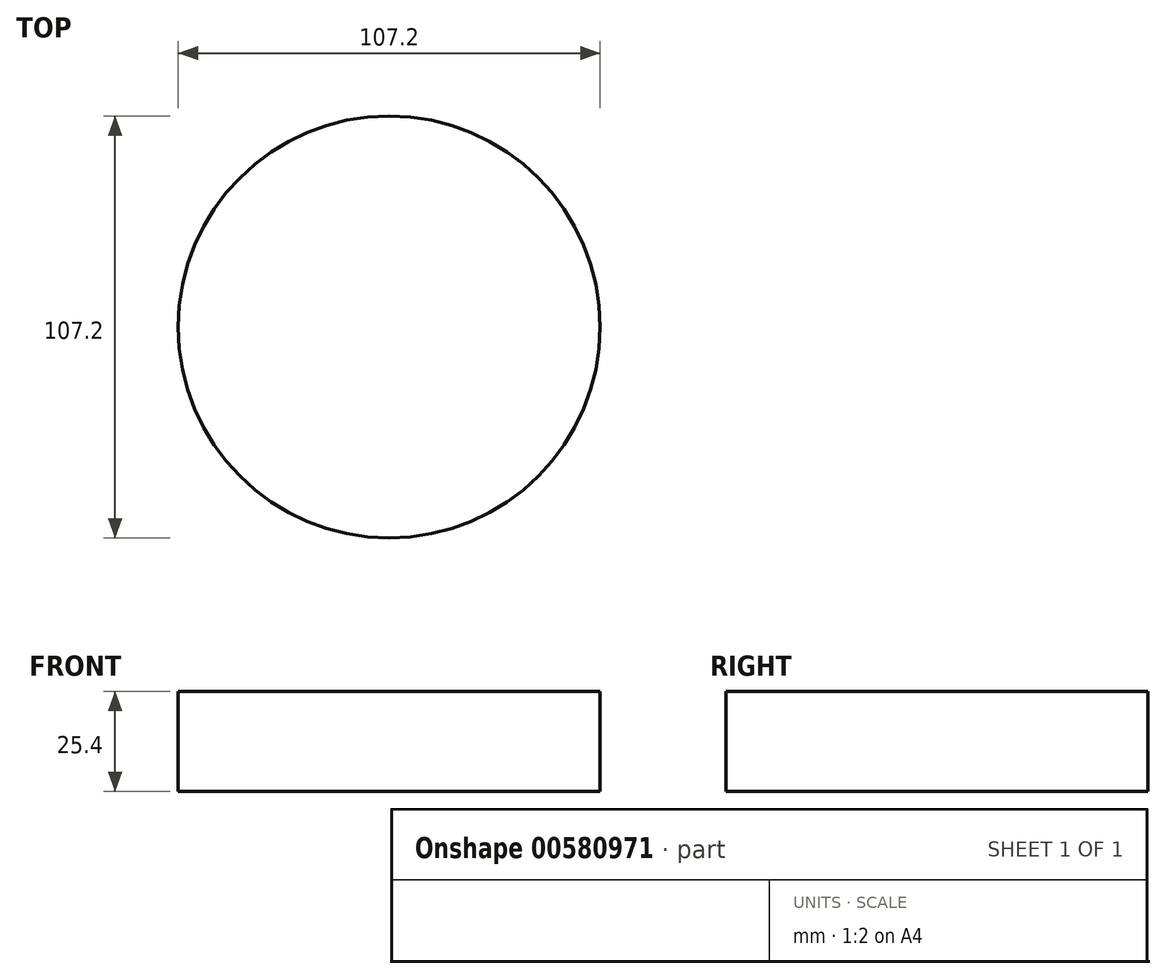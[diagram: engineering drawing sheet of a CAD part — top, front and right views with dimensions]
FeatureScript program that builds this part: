
annotation { "Feature Type Name" : "Feature", "Feature Type Description" : "" }
export const myFeature = defineFeature(function(context is Context, id is Id, definition is map)
    precondition{}
    {
        {
            var Q0;
            Q0=qCreatedBy(makeId("Top.planeOp"),FACE);
            var sketch = newSketch(context, id + "F0", { "sketchPlane" : qUnion([Q0])});
            skCircle(sketch, "E0", {"center": v(0, 0) * mm, "radius": 53.6 * mm});
            skSolve(sketch);
        }
        {
            var Q0;
            Q0=makeQuery(id+"F0.imprint","IMPRINT",FACE,{"disambiguationData":[TD([[makeQuery(id+"F0.imprint","IMPRINT",EDGE,{"derivedFrom":sQuery(id+"F0.wireOp",EDGE,"E0")}),1.0]])]});
            extrude(context, id + "F1", {"entities" : qUnion([Q0]), "depth" : 25.4 * mm, "offsetDistance" : 25.4 * mm});
        }
    });
